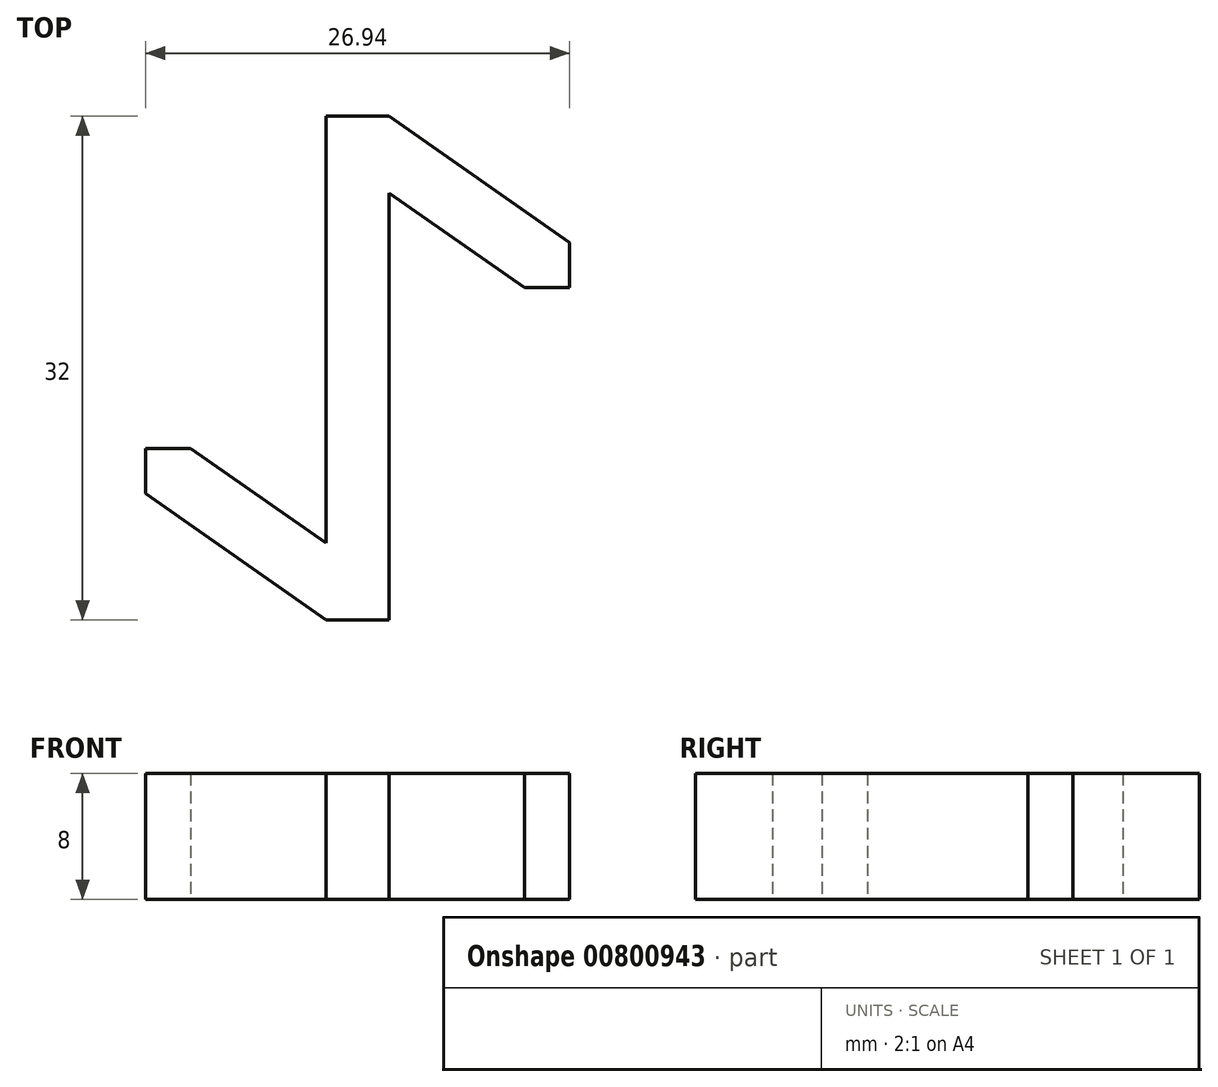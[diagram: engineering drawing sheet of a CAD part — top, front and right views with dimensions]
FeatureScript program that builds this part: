
annotation { "Feature Type Name" : "Feature", "Feature Type Description" : "" }
export const myFeature = defineFeature(function(context is Context, id is Id, definition is map)
    precondition{}
    {
        {
            var Q0;
            Q0=qCreatedBy(makeId("Top.planeOp"),FACE);
            var sketch = newSketch(context, id + "F0", { "sketchPlane" : qUnion([Q0])});
            skLineSegment(sketch, "E0", {"start": v(0, 0) * mm, "end": v(0, -27.12) * mm});
            skLineSegment(sketch, "E1", {"start": v(0, -27.12) * mm, "end": v(-8.6, -21.1) * mm});
            skLineSegment(sketch, "E2", {"start": v(-8.6, -21.1) * mm, "end": v(-11.47, -21.1) * mm});
            skLineSegment(sketch, "E3", {"start": v(-11.47, -21.1) * mm, "end": v(-11.47, -23.97) * mm});
            skLineSegment(sketch, "E4", {"start": v(-11.47, -23.97) * mm, "end": v(0, -32) * mm});
            skLineSegment(sketch, "E5", {"start": v(0, -32) * mm, "end": v(4, -32) * mm});
            skLineSegment(sketch, "E6", {"start": v(4, -32) * mm, "end": v(4, -4.88) * mm});
            skLineSegment(sketch, "E7", {"start": v(4, -4.88) * mm, "end": v(12.6, -10.9) * mm});
            skLineSegment(sketch, "E8", {"start": v(12.6, -10.9) * mm, "end": v(15.47, -10.9) * mm});
            skLineSegment(sketch, "E9", {"start": v(15.47, -10.9) * mm, "end": v(15.47, -8.03) * mm});
            skLineSegment(sketch, "E10", {"start": v(15.47, -8.03) * mm, "end": v(4, 0) * mm});
            skLineSegment(sketch, "E11", {"start": v(4, 0) * mm, "end": v(0, 0) * mm});
            skSolve(sketch);
        }
        {
            var Q0;
            Q0=makeQuery(id+"F0.imprint","IMPRINT",FACE,{"disambiguationData":[TD([[makeQuery(id+"F0.imprint","IMPRINT",EDGE,{"derivedFrom":sQuery(id+"F0.wireOp",EDGE,"E0")}),1.0]])]});
            extrude(context, id + "F1", {"entities" : qUnion([Q0]), "depth" : 8 * mm, "offsetDistance" : 25 * mm});
        }
    });
